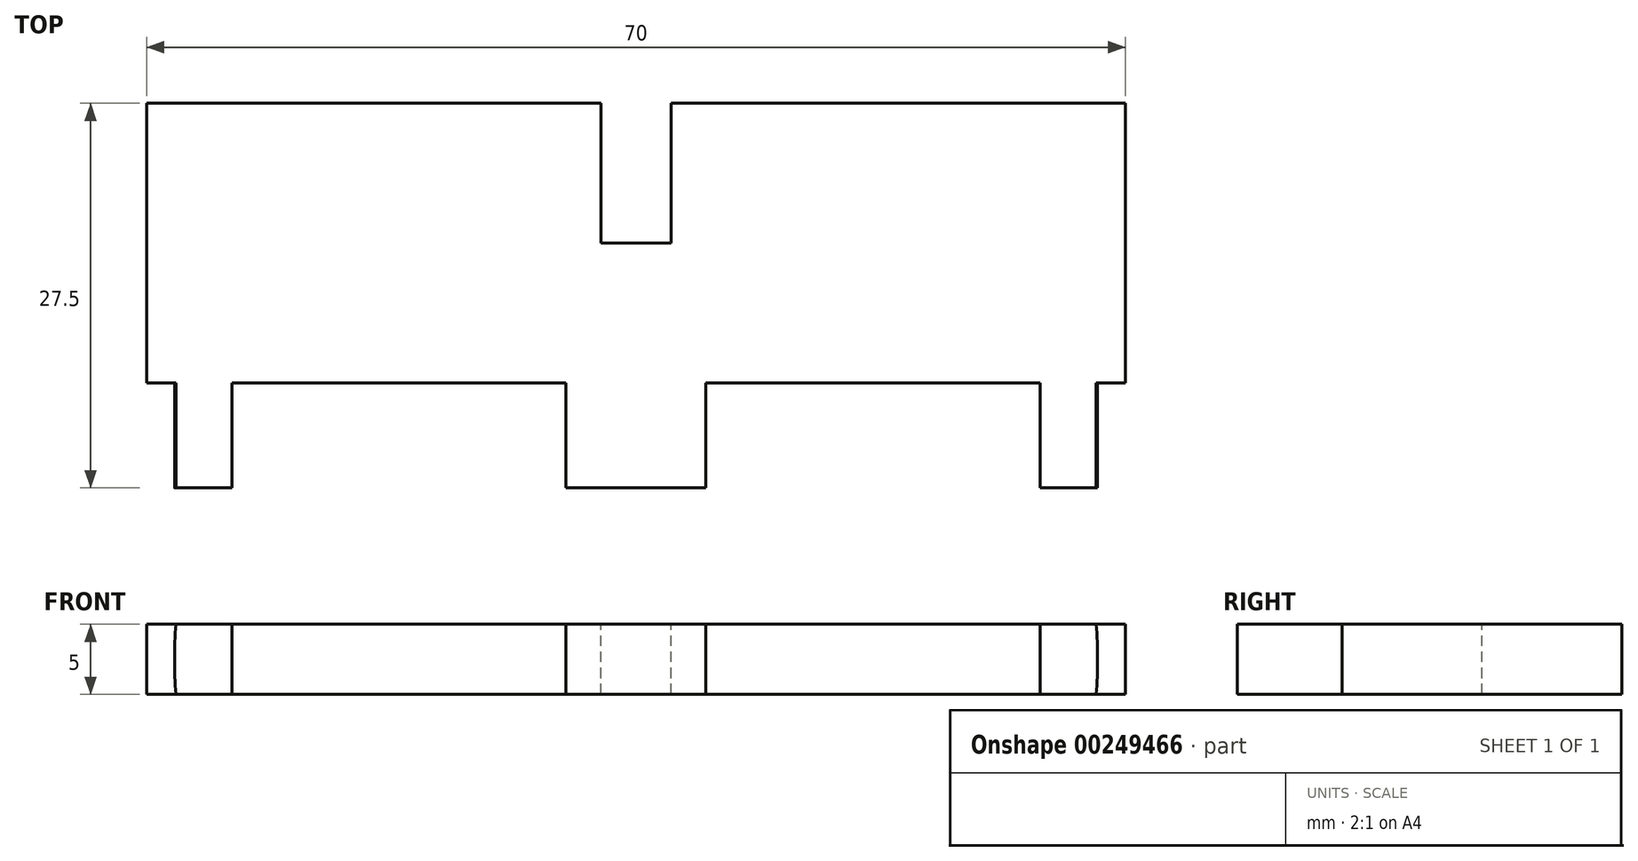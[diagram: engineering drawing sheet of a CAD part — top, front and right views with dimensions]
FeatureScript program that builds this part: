
annotation { "Feature Type Name" : "Feature", "Feature Type Description" : "" }
export const myFeature = defineFeature(function(context is Context, id is Id, definition is map)
    precondition{}
    {
        {
            var Q0;
            Q0=qCreatedBy(makeId("Front.planeOp"),FACE);
            var sketch = newSketch(context, id + "F0", { "sketchPlane" : qUnion([Q0])});
            skLineSegment(sketch, "E0.bottom", {"start": v(-35, 2.5) * mm, "end": v(35, 2.5) * mm});
            skLineSegment(sketch, "E0.top", {"start": v(-35, -2.5) * mm, "end": v(35, -2.5) * mm});
            skLineSegment(sketch, "E0.left", {"start": v(-35, 2.5) * mm, "end": v(-35, -2.5) * mm});
            skLineSegment(sketch, "E0.right", {"start": v(35, 2.5) * mm, "end": v(35, -2.5) * mm});
            skPoint(sketch, "E0.middle", {"position": v(0, 0) * mm});
            skSolve(sketch);
        }
        {
            var Q0;
            Q0 = qSketchRegion(id + "F0", true);
            extrude(context, id + "F1", {"entities" : qUnion([Q0]), "depth" : 20 * mm});
        }
        {
            var Q0;
            Q0=qCreatedBy(makeId("Front.planeOp"),FACE);
            var sketch = newSketch(context, id + "F2", { "sketchPlane" : qUnion([Q0])});
            skArc(sketch, "E1", {"start": v(32.9, -2.5) * mm, "mid": v(33, 0) * mm, "end": v(32.9, 2.5) * mm});
            skLineSegment(sketch, "E2", {"start": v(-32.9, 2.5) * mm, "end": v(-28.9, 2.5) * mm});
            skLineSegment(sketch, "E3", {"start": v(-28.9, 2.5) * mm, "end": v(-28.9, -2.5) * mm});
            skLineSegment(sketch, "E4", {"start": v(-32.9, -2.5) * mm, "end": v(-28.9, -2.5) * mm});
            skLineSegment(sketch, "E5", {"start": v(32.9, -2.5) * mm, "end": v(28.9, -2.5) * mm});
            skLineSegment(sketch, "E6", {"start": v(28.9, -2.5) * mm, "end": v(28.9, 2.5) * mm});
            skLineSegment(sketch, "E7", {"start": v(28.9, 2.5) * mm, "end": v(32.9, 2.5) * mm});
            skLineSegment(sketch, "E8.bottom", {"start": v(5, -2.5) * mm, "end": v(-5, -2.5) * mm});
            skLineSegment(sketch, "E8.top", {"start": v(5, 2.5) * mm, "end": v(-5, 2.5) * mm});
            skLineSegment(sketch, "E8.left", {"start": v(5, -2.5) * mm, "end": v(5, 2.5) * mm});
            skLineSegment(sketch, "E8.right", {"start": v(-5, -2.5) * mm, "end": v(-5, 2.5) * mm});
            skArc(sketch, "E9.trimOffspring", {"start": v(-32.9, 2.5) * mm, "mid": v(-33, 0) * mm, "end": v(-32.9, -2.5) * mm});
            skSolve(sketch);
        }
        {
            var Q0;
            Q0 = qSketchRegion(id + "F2", true);
            extrude(context, id + "F3", {"entities" : qUnion([Q0]), "operationType" : NewBodyOperationType.ADD, "depth" : 27.5 * mm});
        }
        {
            var Q0;
            Q0=qCreatedBy(makeId("Top.planeOp"),FACE);
            var sketch = newSketch(context, id + "F4", { "sketchPlane" : qUnion([Q0])});
            skLineSegment(sketch, "E10", {"start": v(0, 0) * mm, "end": v(2.5, 0) * mm});
            skLineSegment(sketch, "E11", {"start": v(0, 0) * mm, "end": v(-2.5, 0) * mm});
            skLineSegment(sketch, "E12", {"start": v(2.5, 0) * mm, "end": v(2.5, -10) * mm});
            skLineSegment(sketch, "E13", {"start": v(-2.5, 0) * mm, "end": v(-2.5, -10) * mm});
            skLineSegment(sketch, "E14", {"start": v(2.5, -10) * mm, "end": v(-2.5, -10) * mm});
            skSolve(sketch);
        }
        {
            var Q0;
            Q0 = qSketchRegion(id + "F4", true);
            extrude(context, id + "F5", {"entities" : qUnion([Q0]), "operationType" : NewBodyOperationType.REMOVE, "endBound" : BoundingType.THROUGH_ALL, "oppositeDirection" : true, "depth" : 25 * mm});
        }
        {
            var Q0;
            Q0 = qSketchRegion(id + "F4", true);
            extrude(context, id + "F6", {"entities" : qUnion([Q0]), "operationType" : NewBodyOperationType.REMOVE, "endBound" : BoundingType.THROUGH_ALL, "depth" : 25 * mm});
        }
    });
